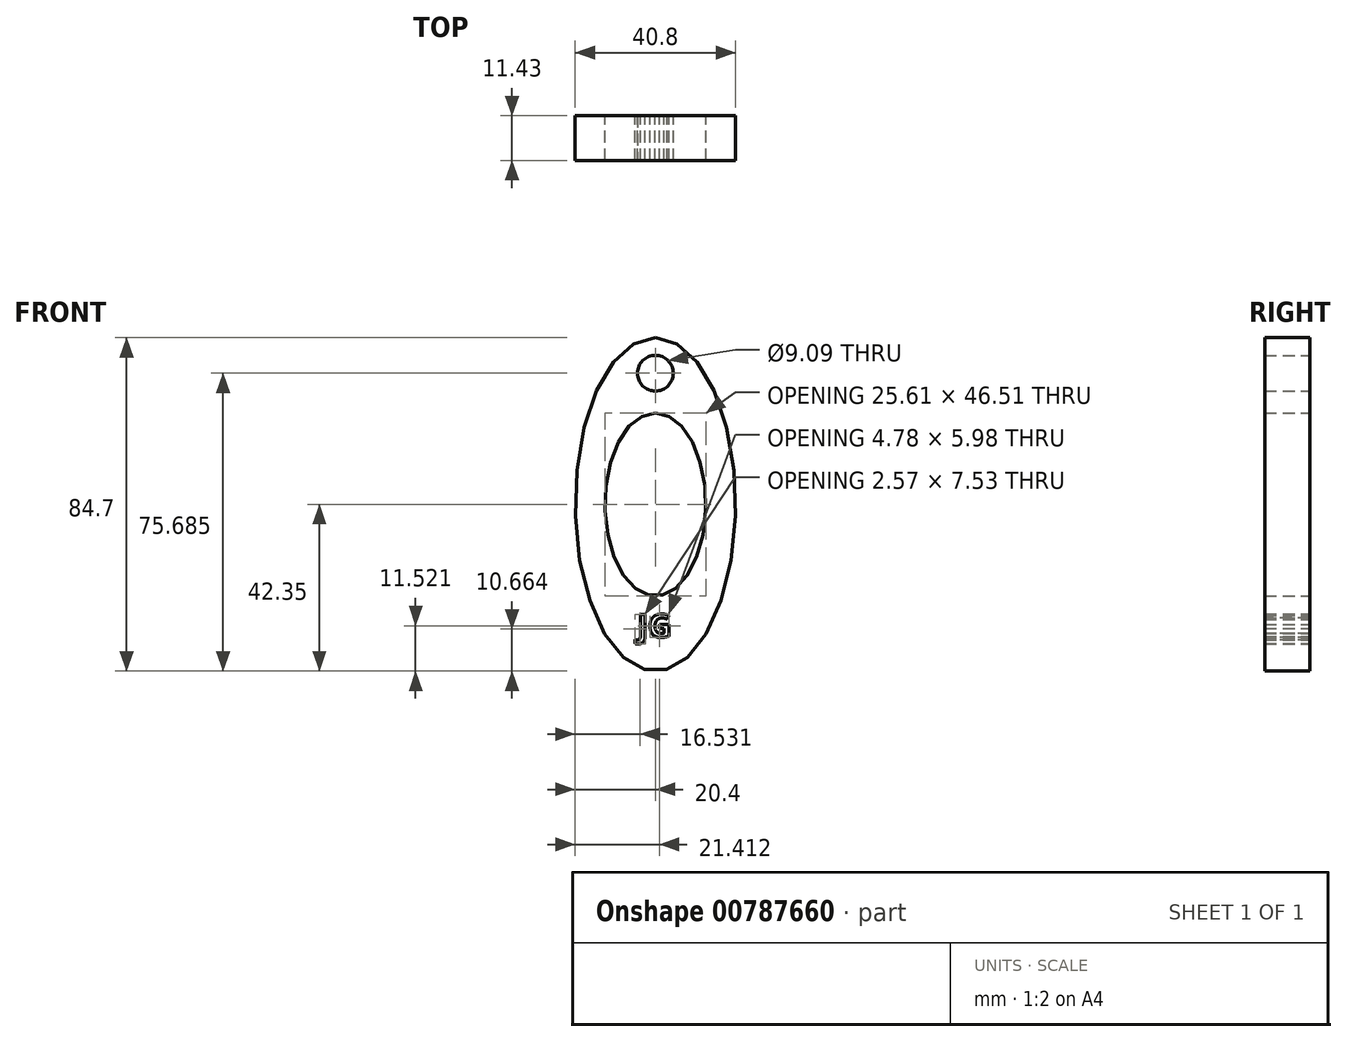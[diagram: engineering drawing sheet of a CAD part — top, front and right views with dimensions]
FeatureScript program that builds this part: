
annotation { "Feature Type Name" : "Feature", "Feature Type Description" : "" }
export const myFeature = defineFeature(function(context is Context, id is Id, definition is map)
    precondition{}
    {
        {
            var Q0;
            Q0=qCreatedBy(makeId("Front.planeOp"),FACE);
            var sketch = newSketch(context, id + "F0", { "sketchPlane" : qUnion([Q0])});
            skEllipse(sketch, "E0", {"center": v(0, 0) * mm, "majorRadius": 42.35 * mm, "minorRadius": 20.4 * mm, "majorAxis": v(0, 1)});
            skEllipse(sketch, "E1", {"center": v(0, 0) * mm, "majorRadius": 23.25 * mm, "minorRadius": 12.8 * mm, "majorAxis": v(0, 1)});
            skText(sketch, "E2", { "text": "JG", "fontName": "OpenSans-Bold.ttf"});
            skCircle(sketch, "E3", {"center": v(0, 33.33) * mm, "radius": 4.55 * mm});
            const initialGuessF0  = {"E2": [-0.00455, -0.03374, 1, 0, 0.00587]};
            skSetInitialGuess(sketch, initialGuessF0);
            skSolve(sketch);
        }
        {
            var Q0;
            Q0=makeQuery(id+"F0.imprint","IMPRINT",FACE,{"disambiguationData":[TD([[makeQuery(id+"F0.imprint","IMPRINT",EDGE,{"derivedFrom":sQuery(id+"F0.wireOp",EDGE,"E0")}),1.0]])]});
            extrude(context, id + "F1", {"entities" : qUnion([Q0]), "depth" : 11.43 * mm, "offsetDistance" : 25.4 * mm});
        }
    });
